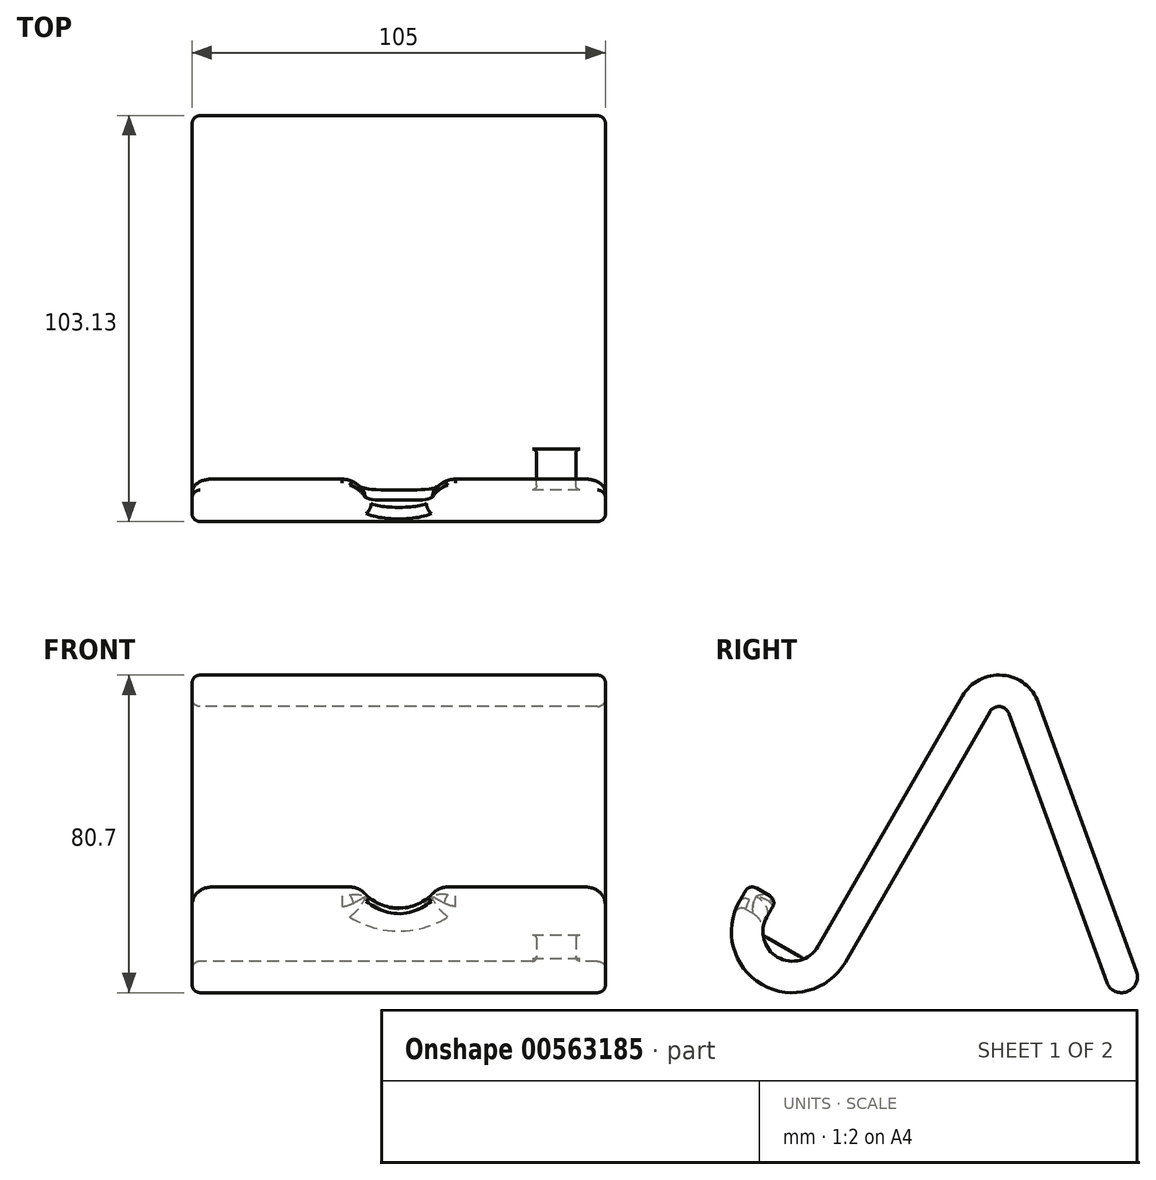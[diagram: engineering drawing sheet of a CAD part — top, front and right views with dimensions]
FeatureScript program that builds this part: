
annotation { "Feature Type Name" : "Feature", "Feature Type Description" : "" }
export const myFeature = defineFeature(function(context is Context, id is Id, definition is map)
    precondition{}
    {
        {
            var Q0;
            Q0=qCreatedBy(makeId("Right.planeOp"),FACE);
            var sketch = newSketch(context, id + "F0", { "sketchPlane" : qUnion([Q0])});
            skLineSegment(sketch, "E0", {"start": v(13.42, 7.75) * mm, "end": v(50.14, 71.35) * mm});
            skArc(sketch, "E1", {"start": v(50.14, 71.35) * mm, "mid": v(52.72, 72.69) * mm, "end": v(55.02, 70.92) * mm});
            skLineSegment(sketch, "E2", {"start": v(55.02, 70.92) * mm, "end": v(79.87, 2.63) * mm});
            skArc(sketch, "E3", {"start": v(13.42, 7.75) * mm, "mid": v(-7.75, 2.08) * mm, "end": v(-13.42, 23.25) * mm});
            skArc(sketch, "E4", {"start": v(79.87, 2.63) * mm, "mid": v(85, 0.24) * mm, "end": v(87.4, 5.37) * mm});
            skLineSegment(sketch, "E5", {"start": v(87.4, 5.37) * mm, "end": v(62.53, 73.66) * mm});
            skArc(sketch, "E6", {"start": v(62.53, 73.66) * mm, "mid": v(53.41, 80.66) * mm, "end": v(43.21, 75.35) * mm});
            skLineSegment(sketch, "E7", {"start": v(43.21, 75.35) * mm, "end": v(6.5, 11.75) * mm});
            skLineSegment(sketch, "E8", {"start": v(0, 0) * mm, "end": v(85, 0) * mm, "construction": true});
            skPoint(sketch, "E8.endSnap0", {"position": v(85, 0.24) * mm});
            skArc(sketch, "E9", {"start": v(6.5, 11.75) * mm, "mid": v(-3.75, 9) * mm, "end": v(-6.5, 19.25) * mm});
            skLineSegment(sketch, "E10", {"start": v(-6.5, 19.25) * mm, "end": v(-4, 23.58) * mm});
            skLineSegment(sketch, "E11", {"start": v(-13.42, 23.25) * mm, "end": v(-10.92, 27.58) * mm});
            skLineSegment(sketch, "E12", {"start": v(-10.92, 27.58) * mm, "end": v(-4, 23.58) * mm});
            skLineSegment(sketch, "E13", {"start": v(52.48, 70) * mm, "end": v(52.48, 0) * mm, "construction": true});
            skSolve(sketch);
        }
        {
            var Q0;
            Q0 = qSketchRegion(id + "F0", true);
            extrude(context, id + "F1", {"entities" : qUnion([Q0]), "endBound" : BoundingType.SYMMETRIC, "depth" : 105 * mm, "offsetDistance" : 25 * mm});
        }
        {
            var Q0;
            Q0=makeQuery(id+"F1.opExtrude","SWEPT_FACE",FACE,{"disambiguationData":[OSD([sQuery(id+"F0.wireOp",EDGE,"E11")])]});
            var sketch = newSketch(context, id + "F2", { "sketchPlane" : qUnion([Q0])});
            skArc(sketch, "E14", {"start": v(-9.8, 18.42) * mm, "mid": v(0, 12.42) * mm, "end": v(9.8, 18.42) * mm});
            skLineSegment(sketch, "E15", {"start": v(-9.8, 18.42) * mm, "end": v(9.8, 18.42) * mm});
            skSolve(sketch);
        }
        {
            var Q0;
            Q0 = qSketchRegion(id + "F2", true);
            extrude(context, id + "F3", {"entities" : qUnion([Q0]), "operationType" : NewBodyOperationType.REMOVE, "endBound" : BoundingType.UP_TO_NEXT, "oppositeDirection" : true, "depth" : 25 * mm, "offsetDistance" : 25 * mm});
        }
        {
            var Q0;
            Q0=qCreatedBy(makeId("Right.planeOp"),FACE);
            cPlane(context, id + "F4", {"entities" : qUnion([Q0]), "cplaneType" : CPlaneType.OFFSET, "offset" : 45 * mm, "width" : 150 * mm, "height" : 150 * mm});
        }
        {
            var Q0;
            Q0=qCreatedBy(id+"F4.planeOp",FACE);
            var sketch = newSketch(context, id + "F5", { "sketchPlane" : qUnion([Q0])});
            skLineSegment(sketch, "E16", {"start": v(-8.75, 15.35) * mm, "end": v(4.25, 7.85) * mm});
            skLineSegment(sketch, "E17", {"start": v(-8.75, 15.35) * mm, "end": v(-10.75, 11.89) * mm});
            skLineSegment(sketch, "E18", {"start": v(-10.75, 11.89) * mm, "end": v(2.25, 4.39) * mm});
            skLineSegment(sketch, "E19", {"start": v(2.25, 4.39) * mm, "end": v(4.25, 7.85) * mm});
            skSolve(sketch);
        }
        {
            var Q0;
            Q0=makeQuery(id+"F1.opExtrude","CAP_EDGE",EDGE,{"disambiguationData":[OSD([sQuery(id+"F0.wireOp",EDGE,"E12")])],"isStart":true});
            var Q1;
            Q1=makeQuery(id+"F1.opExtrude","CAP_EDGE",EDGE,{"disambiguationData":[OSD([sQuery(id+"F0.wireOp",EDGE,"E12")])],"isStart":false});
            fillet(context, id + "F6", {"entities" : qUnion([Q0, Q1]), "radius" : 5 * mm, "tangentPropagation" : true, "allowEdgeOverflow" : false});
        }
        {
            var Q0;
            {var subQ0=sQuery(id+"F0.wireOp",EDGE,"E12");var subQ1=sQuery(id+"F0.wireOp",EDGE,"E11");Q0=makeQuery(id+"F3.boolean.opBoolean","SPLIT",EDGE,{"disambiguationData":[TD([makeQuery(id+"F1.opExtrude","CAP_FACE",FACE,{"disambiguationData":[OSD([sQuery(id+"F0.wireOp",EDGE,"E0"),sQuery(id+"F0.wireOp",EDGE,"E1"),sQuery(id+"F0.wireOp",EDGE,"E2"),sQuery(id+"F0.wireOp",EDGE,"E3"),sQuery(id+"F0.wireOp",EDGE,"E4"),sQuery(id+"F0.wireOp",EDGE,"E5"),sQuery(id+"F0.wireOp",EDGE,"E6"),sQuery(id+"F0.wireOp",EDGE,"E7"),sQuery(id+"F0.wireOp",EDGE,"E9"),sQuery(id+"F0.wireOp",EDGE,"E10"),subQ1,subQ0])],"isStart":true})])],"derivedFrom":makeQuery(id+"F1.opExtrude","SWEPT_EDGE",EDGE,{"disambiguationData":[OSD([subQ1,subQ0])]})});}
            var Q1;
            Q1=makeQuery(id+"F3.boolean.opBoolean","COPY",EDGE,{"derivedFrom":makeQuery(id+"F3.opExtrude","CAP_EDGE",EDGE,{"disambiguationData":[OSD([sQuery(id+"F2.wireOp",EDGE,"E14")])],"isStart":true})});
            var Q2;
            {var subQ0=sQuery(id+"F0.wireOp",EDGE,"E12");var subQ1=sQuery(id+"F0.wireOp",EDGE,"E11");Q2=makeQuery(id+"F3.boolean.opBoolean","SPLIT",EDGE,{"disambiguationData":[TD([makeQuery(id+"F1.opExtrude","CAP_FACE",FACE,{"disambiguationData":[OSD([sQuery(id+"F0.wireOp",EDGE,"E0"),sQuery(id+"F0.wireOp",EDGE,"E1"),sQuery(id+"F0.wireOp",EDGE,"E2"),sQuery(id+"F0.wireOp",EDGE,"E3"),sQuery(id+"F0.wireOp",EDGE,"E4"),sQuery(id+"F0.wireOp",EDGE,"E5"),sQuery(id+"F0.wireOp",EDGE,"E6"),sQuery(id+"F0.wireOp",EDGE,"E7"),sQuery(id+"F0.wireOp",EDGE,"E9"),sQuery(id+"F0.wireOp",EDGE,"E10"),subQ1,subQ0])],"isStart":false})])],"derivedFrom":makeQuery(id+"F1.opExtrude","SWEPT_EDGE",EDGE,{"disambiguationData":[OSD([subQ1,subQ0])]})});}
            var Q3;
            {var subQ0=sQuery(id+"F0.wireOp",EDGE,"E12");var subQ1=sQuery(id+"F0.wireOp",EDGE,"E10");Q3=makeQuery(id+"F3.boolean.opBoolean","SPLIT",EDGE,{"disambiguationData":[TD([makeQuery(id+"F1.opExtrude","CAP_FACE",FACE,{"disambiguationData":[OSD([sQuery(id+"F0.wireOp",EDGE,"E0"),sQuery(id+"F0.wireOp",EDGE,"E1"),sQuery(id+"F0.wireOp",EDGE,"E2"),sQuery(id+"F0.wireOp",EDGE,"E3"),sQuery(id+"F0.wireOp",EDGE,"E4"),sQuery(id+"F0.wireOp",EDGE,"E5"),sQuery(id+"F0.wireOp",EDGE,"E6"),sQuery(id+"F0.wireOp",EDGE,"E7"),sQuery(id+"F0.wireOp",EDGE,"E9"),subQ1,sQuery(id+"F0.wireOp",EDGE,"E11"),subQ0])],"isStart":true})])],"derivedFrom":makeQuery(id+"F1.opExtrude","SWEPT_EDGE",EDGE,{"disambiguationData":[OSD([subQ1,subQ0])]})});}
            var Q4;
            Q4=makeQuery(id+"F3.boolean.opBoolean","COPY",EDGE,{"derivedFrom":makeQuery(id+"F3.opExtrude","TWEAK_EDGE",EDGE,{"derivedFrom":[makeQuery(id+"F1.opExtrude","SWEPT_FACE",FACE,{"disambiguationData":[OSD([sQuery(id+"F0.wireOp",EDGE,"E10")])]}),makeQuery(id+"F2.imprint","IMPRINT",EDGE,{"derivedFrom":sQuery(id+"F2.wireOp",EDGE,"E14")})]})});
            var Q5;
            {var subQ0=sQuery(id+"F0.wireOp",EDGE,"E12");var subQ1=sQuery(id+"F0.wireOp",EDGE,"E10");Q5=makeQuery(id+"F3.boolean.opBoolean","SPLIT",EDGE,{"disambiguationData":[TD([makeQuery(id+"F1.opExtrude","CAP_FACE",FACE,{"disambiguationData":[OSD([sQuery(id+"F0.wireOp",EDGE,"E0"),sQuery(id+"F0.wireOp",EDGE,"E1"),sQuery(id+"F0.wireOp",EDGE,"E2"),sQuery(id+"F0.wireOp",EDGE,"E3"),sQuery(id+"F0.wireOp",EDGE,"E4"),sQuery(id+"F0.wireOp",EDGE,"E5"),sQuery(id+"F0.wireOp",EDGE,"E6"),sQuery(id+"F0.wireOp",EDGE,"E7"),sQuery(id+"F0.wireOp",EDGE,"E9"),subQ1,sQuery(id+"F0.wireOp",EDGE,"E11"),subQ0])],"isStart":false})])],"derivedFrom":makeQuery(id+"F1.opExtrude","SWEPT_EDGE",EDGE,{"disambiguationData":[OSD([subQ1,subQ0])]})});}
            fillet(context, id + "F7", {"entities" : qUnion([Q0, Q1, Q2, Q3, Q4, Q5]), "radius" : 2 * mm, "tangentPropagation" : true, "allowEdgeOverflow" : false});
        }
        {
            var Q0;
            Q0 = qSketchRegion(id + "F5", true);
            extrude(context, id + "F8", {"entities" : qUnion([Q0]), "operationType" : NewBodyOperationType.ADD, "oppositeDirection" : true, "depth" : 10 * mm, "offsetDistance" : 25 * mm});
        }
        {
            var Q0;
            {var subQ0=sQuery(id+"F2.wireOp",EDGE,"E15");var subQ1=sQuery(id+"F2.wireOp",EDGE,"E14");var subQ2=sQuery(id+"F0.wireOp",EDGE,"E12");var subQ3=sQuery(id+"F0.wireOp",EDGE,"E11");Q0=makeQuery(id+"F3.boolean.opBoolean","COPY",EDGE,{"derivedFrom":makeQuery(id+"F3.opExtrude","SWEPT_EDGE",EDGE,{"disambiguationData":[OSD([subQ3,subQ2,subQ1,subQ0]),TDD([makeQuery(id+"F2.imprint","INTERSECT",VERTEX,{"disambiguationData":[OD(1.0)],"derivedFrom":[makeQuery(id+"F1.opExtrude","SWEPT_EDGE",EDGE,{"disambiguationData":[OSD([subQ3,subQ2])]}),subQ1,subQ0]})])]})});}
            var Q1;
            {var subQ0=sQuery(id+"F2.wireOp",EDGE,"E15");var subQ1=sQuery(id+"F2.wireOp",EDGE,"E14");var subQ2=sQuery(id+"F0.wireOp",EDGE,"E12");var subQ3=sQuery(id+"F0.wireOp",EDGE,"E11");Q1=makeQuery(id+"F3.boolean.opBoolean","COPY",EDGE,{"derivedFrom":makeQuery(id+"F3.opExtrude","SWEPT_EDGE",EDGE,{"disambiguationData":[OSD([subQ3,subQ2,subQ1,subQ0]),TDD([makeQuery(id+"F2.imprint","INTERSECT",VERTEX,{"disambiguationData":[OD(0.0)],"derivedFrom":[makeQuery(id+"F1.opExtrude","SWEPT_EDGE",EDGE,{"disambiguationData":[OSD([subQ3,subQ2])]}),subQ1,subQ0]})])]})});}
            fillet(context, id + "F9", {"entities" : qUnion([Q0, Q1]), "radius" : 5 * mm, "tangentPropagation" : true, "allowEdgeOverflow" : false});
        }
        {
            var Q0;
            Q0=makeQuery(id+"FRa4or2CdPa2jjW_1.1.F8.boolean.opBoolean","INTERSECT",EDGE,{"derivedFrom":[makeQuery(id+"F1.opExtrude","SWEPT_FACE",FACE,{"disambiguationData":[OSD([sQuery(id+"F0.wireOp",EDGE,"E9")])]}),makeQuery(id+"FRa4or2CdPa2jjW_1.1.F8.opExtrude","CAP_FACE",FACE,{"disambiguationData":[OSD([sQuery(id+"F5.wireOp",EDGE,"E16"),sQuery(id+"F5.wireOp",EDGE,"E17"),sQuery(id+"F5.wireOp",EDGE,"E18"),sQuery(id+"F5.wireOp",EDGE,"E19")])],"isStart":true})]});
            var Q1;
            Q1=makeQuery(id+"FRa4or2CdPa2jjW_1.1.F8.boolean.opBoolean","INTERSECT",EDGE,{"derivedFrom":[makeQuery(id+"F1.opExtrude","SWEPT_FACE",FACE,{"disambiguationData":[OSD([sQuery(id+"F0.wireOp",EDGE,"E9")])]}),makeQuery(id+"FRa4or2CdPa2jjW_1.1.F8.opExtrude","CAP_FACE",FACE,{"disambiguationData":[OSD([sQuery(id+"F5.wireOp",EDGE,"E16"),sQuery(id+"F5.wireOp",EDGE,"E17"),sQuery(id+"F5.wireOp",EDGE,"E18"),sQuery(id+"F5.wireOp",EDGE,"E19")])],"isStart":false})]});
            var Q2;
            Q2=makeQuery(id+"F8.boolean.opBoolean","INTERSECT",EDGE,{"derivedFrom":[makeQuery(id+"F1.opExtrude","SWEPT_FACE",FACE,{"disambiguationData":[OSD([sQuery(id+"F0.wireOp",EDGE,"E9")])]}),makeQuery(id+"F8.opExtrude","CAP_FACE",FACE,{"disambiguationData":[OSD([sQuery(id+"F5.wireOp",EDGE,"E16"),sQuery(id+"F5.wireOp",EDGE,"E17"),sQuery(id+"F5.wireOp",EDGE,"E18"),sQuery(id+"F5.wireOp",EDGE,"E19")])],"isStart":true})]});
            var Q3;
            Q3=makeQuery(id+"F8.boolean.opBoolean","INTERSECT",EDGE,{"derivedFrom":[makeQuery(id+"F1.opExtrude","SWEPT_FACE",FACE,{"disambiguationData":[OSD([sQuery(id+"F0.wireOp",EDGE,"E9")])]}),makeQuery(id+"F8.opExtrude","CAP_FACE",FACE,{"disambiguationData":[OSD([sQuery(id+"F5.wireOp",EDGE,"E16"),sQuery(id+"F5.wireOp",EDGE,"E17"),sQuery(id+"F5.wireOp",EDGE,"E18"),sQuery(id+"F5.wireOp",EDGE,"E19")])],"isStart":false})]});
            fillet(context, id + "F10", {"entities" : qUnion([Q0, Q1, Q2, Q3]), "radius" : 1 * mm, "tangentPropagation" : true, "allowEdgeOverflow" : false});
        }
    });
